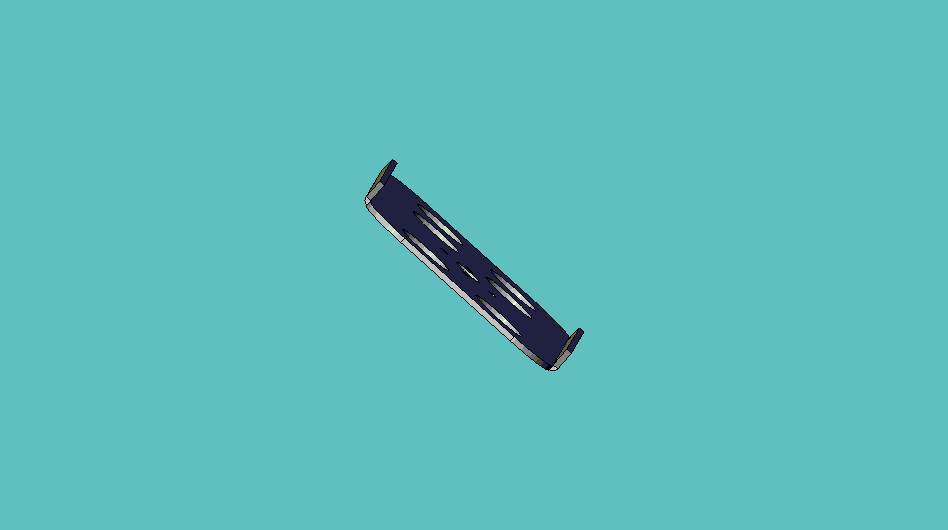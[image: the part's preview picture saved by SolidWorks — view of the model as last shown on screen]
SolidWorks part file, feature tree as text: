
SOLIDWORKS PART (.sldprt)
format: sldprt  version: not decoded by parser v0  size: 284,672 bytes
history: native  units: mm
features: sketch x3, extrude x2, material x1, cut_extrude x1, fillet x1 (+12 scaffold rows collapsed)
feature tree (20):
  scaffold x12  (default folders/planes/origin — collapsed)
  material  "Material <not specified>"
  sketch  "Sketch1"  dims[D1=15.875mm]
  extrude  "Extrude1"  Depth=1.524mm
  extrude  "Extrude2"  [1 undecoded]
  sketch  "Sketch1<3>"  dims[D1=6.35mm]
  sketch  "Sketch2"  dims[D1=6.35mm]
  cut_extrude  "Cut-Extrude1"  [1 undecoded]
  fillet  "Fillet1"  Radius=1.5875mm
decode coverage: 5 of 7 modeling features carry decoded parameters
note: 2 parameter values undecoded
note: suppression state not decoded; provenance and decode notes live in map.json
